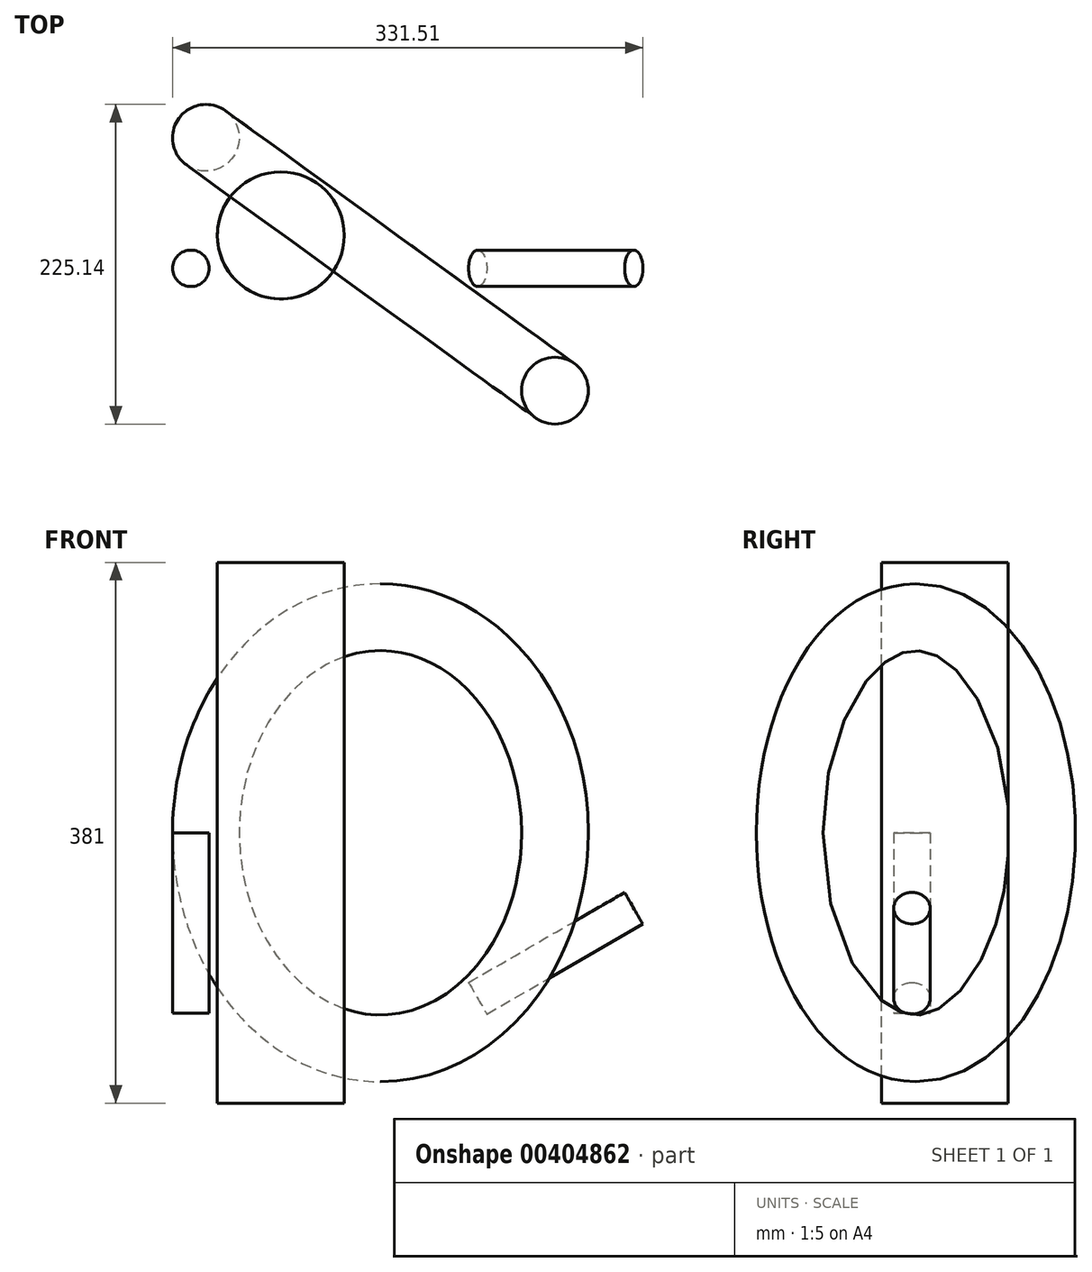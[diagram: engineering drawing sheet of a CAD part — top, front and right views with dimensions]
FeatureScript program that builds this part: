
annotation { "Feature Type Name" : "Feature", "Feature Type Description" : "" }
export const myFeature = defineFeature(function(context is Context, id is Id, definition is map)
    precondition{}
    {
        {
            var Q0;
            Q0=qCreatedBy(makeId("Top.planeOp"),FACE);
            var sketch = newSketch(context, id + "F0", { "sketchPlane" : qUnion([Q0])});
            skCircle(sketch, "E0", {"center": v(6.1, -25.19) * mm, "radius": 44.74 * mm});
            skPoint(sketch, "E0.first.point", {"position": v(-9.34, 16.8) * mm});
            skPoint(sketch, "E0.second.point", {"position": v(50.83, -24.48) * mm});
            skPoint(sketch, "E0.third.point", {"position": v(-38.38, -20.33) * mm});
            skCircle(sketch, "E1", {"center": v(84.33, 14.1) * mm, "radius": 25.52 * mm});
            skPoint(sketch, "E1.first.point", {"position": v(105.6, 0) * mm});
            skPoint(sketch, "E1.second.point", {"position": v(63.07, 0) * mm});
            skPoint(sketch, "E1.third.point", {"position": v(84.44, 39.62) * mm});
            skCircle(sketch, "E2", {"center": v(77.73, -63.99) * mm, "radius": 20.46 * mm});
            skPoint(sketch, "E2.first.point", {"position": v(85.89, -45.23) * mm});
            skPoint(sketch, "E2.second.point", {"position": v(58.09, -69.7) * mm});
            skPoint(sketch, "E2.third.point", {"position": v(57.67, -59.96) * mm});
            skSolve(sketch);
        }
        {
            var Q0;
            Q0=qCreatedBy(makeId("Top.planeOp"),FACE);
            var sketch = newSketch(context, id + "F1", { "sketchPlane" : qUnion([Q0])});
            skLineSegment(sketch, "E3", {"start": v(77.51, -65.04) * mm, "end": v(77.51, -103.23) * mm});
            skSolve(sketch);
        }
        {
            var Q0;
            Q0=qCreatedBy(makeId("Top.planeOp"),FACE);
            var sketch = newSketch(context, id + "F2", { "sketchPlane" : qUnion([Q0])});
            skLineSegment(sketch, "E4", {"start": v(96.06, -18.23) * mm, "end": v(32.39, -106.2) * mm});
            skSolve(sketch);
        }
        {
            var Q0;
            Q0=sQuery(id+"F0.wireOp",EDGE,"E0");
            extrude(context, id + "F3", {"bodyType" : ToolBodyType.SURFACE, "surfaceEntities" : qUnion([Q0]), "endBound" : BoundingType.SYMMETRIC, "depth" : 381 * mm});
        }
        {
            var Q0;
            Q0=qCreatedBy(makeId("Top.planeOp"),FACE);
            var sketch = newSketch(context, id + "F4", { "sketchPlane" : qUnion([Q0])});
            skCircle(sketch, "E5", {"center": v(-46.7, 43.57) * mm, "radius": 23.51 * mm});
            skCircle(sketch, "E6", {"center": v(40.4, 51.6) * mm, "radius": 24.27 * mm});
            skSolve(sketch);
        }
        {
            var Q0;
            Q0=qCreatedBy(makeId("Top.planeOp"),FACE);
            var sketch = newSketch(context, id + "F5", { "sketchPlane" : qUnion([Q0])});
            skCircle(sketch, "E7", {"center": v(-57.23, -48.35) * mm, "radius": 12.85 * mm});
            skPoint(sketch, "E7.first.point", {"position": v(-57.06, -35.5) * mm});
            skPoint(sketch, "E7.second.point", {"position": v(-44.95, -52.13) * mm});
            skPoint(sketch, "E7.third.point", {"position": v(-67.71, -55.78) * mm});
            skSolve(sketch);
        }
        {
            var Q0;
            Q0=sQuery(id+"F4.wireOp",EDGE,"E5");
            var Q1;
            Q1=sQuery(id+"F2.wireOp",EDGE,"E4");
            revolve(context, id + "F6", {"bodyType" : ToolBodyType.SURFACE, "surfaceEntities" : qUnion([Q0]), "axis" : qUnion([Q1]), "revolveType" : RevolveType.FULL});
        }
        {
            var Q0;
            Q0=sQuery(id+"F5.wireOp",EDGE,"E7");
            extrude(context, id + "F7", {"bodyType" : ToolBodyType.SURFACE, "surfaceEntities" : qUnion([Q0]), "oppositeDirection" : true, "depth" : 127 * mm});
        }
        {
            var Q0;
            Q0=makeQuery(id+"F7.opExtrude","SWEPT_BODY",BODY,{"disambiguationData":[OSD([sQuery(id+"F5.wireOp",EDGE,"E7")])]});
            var Q1;
            Q1=sQuery(id+"F1.wireOp",EDGE,"E3");
            transform(context, id + "F8", {"entities" : qUnion([Q0]), "transformType" : TransformType.ROTATION, "transformAxis" : qUnion([Q1]), "angle" : 120 * degree, "makeCopy" : true});
        }
    });
